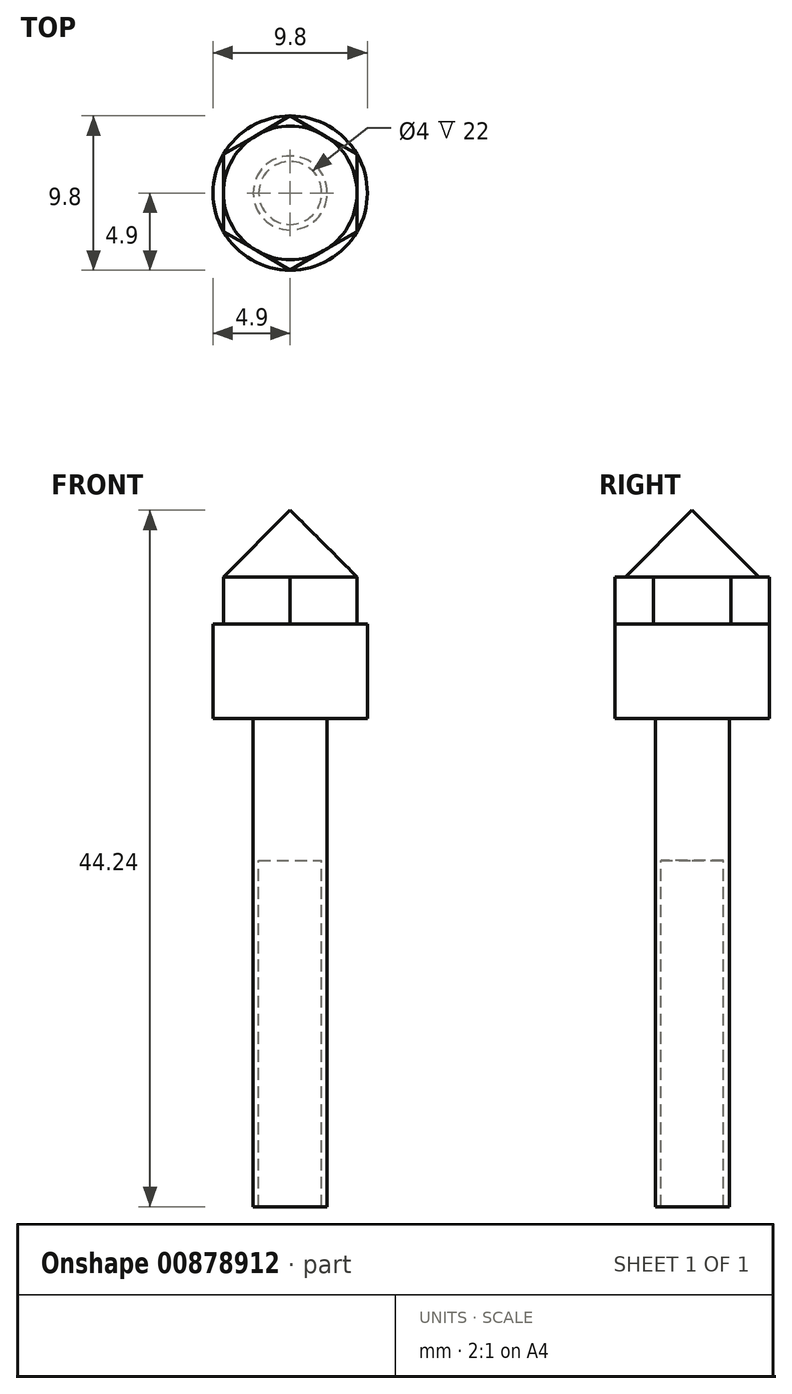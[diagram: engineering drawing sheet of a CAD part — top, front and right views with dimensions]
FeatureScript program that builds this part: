
annotation { "Feature Type Name" : "Feature", "Feature Type Description" : "" }
export const myFeature = defineFeature(function(context is Context, id is Id, definition is map)
    precondition{}
    {
        {
            var Q0;
            Q0=qCreatedBy(makeId("Top.planeOp"),FACE);
            var sketch = newSketch(context, id + "F0", { "sketchPlane" : qUnion([Q0])});
            skCircle(sketch, "E0", {"center": v(0, 0) * mm, "radius": 4.9 * mm});
            skCircle(sketch, "E1", {"center": v(0, 0) * mm, "radius": 2.35 * mm});
            skCircle(sketch, "E2", {"center": v(0, 0) * mm, "radius": 2 * mm});
            skSolve(sketch);
        }
        {
            var Q0;
            Q0=makeQuery(id+"F0.imprint","IMPRINT",FACE,{"disambiguationData":[TD([[makeQuery(id+"F0.imprint","IMPRINT",EDGE,{"derivedFrom":sQuery(id+"F0.wireOp",EDGE,"E0")}),1.0]])]});
            var Q1;
            Q1=makeQuery(id+"F0.imprint","IMPRINT",FACE,{"disambiguationData":[TD([[makeQuery(id+"F0.imprint","IMPRINT",EDGE,{"derivedFrom":sQuery(id+"F0.wireOp",EDGE,"E1")}),1.0]])]});
            var Q2;
            Q2=makeQuery(id+"F0.imprint","IMPRINT",FACE,{"disambiguationData":[TD([[makeQuery(id+"F0.imprint","IMPRINT",EDGE,{"derivedFrom":sQuery(id+"F0.wireOp",EDGE,"E2")}),1.0]])]});
            extrude(context, id + "F1", {"entities" : qUnion([Q0, Q1, Q2]), "depth" : 6 * mm, "offsetDistance" : 25 * mm});
        }
        {
            var Q0;
            Q0=makeQuery(id+"F1.opExtrude","CAP_FACE",FACE,{"disambiguationData":[OSD([sQuery(id+"F0.wireOp",EDGE,"E0")])],"isStart":false});
            var sketch = newSketch(context, id + "F2", { "sketchPlane" : qUnion([Q0])});
            skCircle(sketch, "E3.cCircle", {"center": v(0, 0) * mm, "radius": 4.9 * mm, "construction": true});
            skLineSegment(sketch, "E3.0", {"start": v(0, 4.9) * mm, "end": v(4.24, 2.45) * mm});
            skLineSegment(sketch, "E3.1", {"start": v(4.24, 2.45) * mm, "end": v(4.24, -2.45) * mm});
            skLineSegment(sketch, "E3.2", {"start": v(4.24, -2.45) * mm, "end": v(0, -4.9) * mm});
            skLineSegment(sketch, "E3.3", {"start": v(0, -4.9) * mm, "end": v(-4.24, -2.45) * mm});
            skLineSegment(sketch, "E3.4", {"start": v(-4.24, -2.45) * mm, "end": v(-4.24, 2.45) * mm});
            skLineSegment(sketch, "E3.5", {"start": v(-4.24, 2.45) * mm, "end": v(0, 4.9) * mm});
            skSolve(sketch);
        }
        {
            var Q0;
            Q0=makeQuery(id+"F2.imprint","IMPRINT",FACE,{"disambiguationData":[TD([[makeQuery(id+"F2.imprint","IMPRINT",EDGE,{"derivedFrom":sQuery(id+"F2.wireOp",EDGE,"E3.0")}),-1.0]])]});
            extrude(context, id + "F3", {"entities" : qUnion([Q0]), "operationType" : NewBodyOperationType.ADD, "depth" : 3 * mm, "offsetDistance" : 25 * mm});
        }
        {
            var Q0;
            Q0=makeQuery(id+"F3.opExtrude","CAP_FACE",FACE,{"disambiguationData":[OSD([sQuery(id+"F2.wireOp",EDGE,"E3.0"),sQuery(id+"F2.wireOp",EDGE,"E3.1"),sQuery(id+"F2.wireOp",EDGE,"E3.2"),sQuery(id+"F2.wireOp",EDGE,"E3.3"),sQuery(id+"F2.wireOp",EDGE,"E3.4"),sQuery(id+"F2.wireOp",EDGE,"E3.5")])],"isStart":false});
            var sketch = newSketch(context, id + "F4", { "sketchPlane" : qUnion([Q0])});
            skCircle(sketch, "E4", {"center": v(0, 0) * mm, "radius": 4.24 * mm});
            skSolve(sketch);
        }
        {
            var Q0;
            {var subQ0=sQuery(id+"F4.wireOp",EDGE,"E4");var subQ4=makeQuery(id+"F4.imprint","INTERSECT",VERTEX,{"derivedFrom":[makeQuery(id+"F3.opExtrude","CAP_EDGE",EDGE,{"disambiguationData":[OSD([sQuery(id+"F2.wireOp",EDGE,"E3.0")])],"isStart":false}),subQ0]});Q0=makeQuery(id+"F4.imprint","IMPRINT",FACE,{"disambiguationData":[TD([[makeQuery(id+"F4.imprint","IMPRINT",EDGE,{"disambiguationData":[TD([[subQ4,1.0]])],"derivedFrom":subQ0}),1.0]])]});}
            extrude(context, id + "F5", {"entities" : qUnion([Q0]), "operationType" : NewBodyOperationType.ADD, "depth" : 25 * mm, "offsetDistance" : 25 * mm, "hasDraft" : true, "draftAngle" : 45 * degree, "draftPullDirection" : true});
        }
        {
            var Q0;
            Q0=makeQuery(id+"F0.imprint","IMPRINT",FACE,{"disambiguationData":[TD([[makeQuery(id+"F0.imprint","IMPRINT",EDGE,{"derivedFrom":sQuery(id+"F0.wireOp",EDGE,"E2")}),1.0]])]});
            var Q1;
            Q1=makeQuery(id+"F0.imprint","IMPRINT",FACE,{"disambiguationData":[TD([[makeQuery(id+"F0.imprint","IMPRINT",EDGE,{"derivedFrom":sQuery(id+"F0.wireOp",EDGE,"E1")}),1.0]])]});
            extrude(context, id + "F6", {"entities" : qUnion([Q0, Q1]), "operationType" : NewBodyOperationType.ADD, "oppositeDirection" : true, "depth" : 9 * mm, "offsetDistance" : 25 * mm});
        }
        {
            var Q0;
            Q0=makeQuery(id+"F6.opExtrude","CAP_FACE",FACE,{"disambiguationData":[OSD([sQuery(id+"F0.wireOp",EDGE,"E1")])],"isStart":false});
            var sketch = newSketch(context, id + "F7", { "sketchPlane" : qUnion([Q0])});
            skCircle(sketch, "E5.0", {"center": v(0, 0) * mm, "radius": 2 * mm});
            skSolve(sketch);
        }
        {
            var Q0;
            Q0=makeQuery(id+"F7.imprint","IMPRINT",FACE,{"disambiguationData":[TD([[makeQuery(id+"F7.imprint","IMPRINT",EDGE,{"derivedFrom":sQuery(id+"F7.wireOp",EDGE,"E5.0")}),-1.0]])]});
            extrude(context, id + "F8", {"entities" : qUnion([Q0]), "operationType" : NewBodyOperationType.ADD, "depth" : 22 * mm, "offsetDistance" : 25 * mm});
        }
    });
